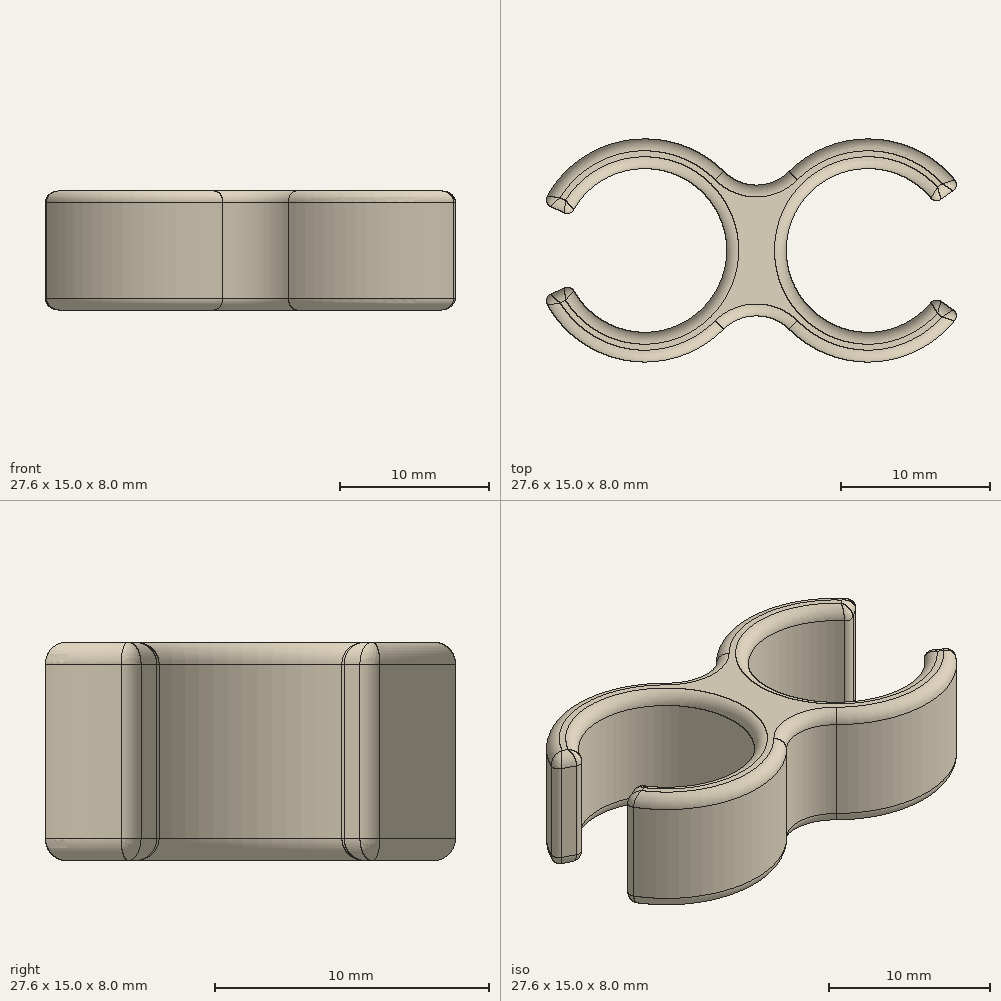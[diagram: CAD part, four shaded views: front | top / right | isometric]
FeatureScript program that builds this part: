
annotation { "Feature Type Name" : "Feature", "Feature Type Description" : "" }
export const myFeature = defineFeature(function(context is Context, id is Id, definition is map)
    precondition{}
    {
        {
            var Q0;
            Q0=qCreatedBy(makeId("Top.planeOp"),FACE);
            var sketch = newSketch(context, id + "F0", { "sketchPlane" : qUnion([Q0])});
            skArc(sketch, "E0", {"start": v(-4.77, -2.73) * mm, "mid": v(5.5, 0) * mm, "end": v(-4.77, 2.73) * mm});
            skArc(sketch, "E1", {"start": v(19.23, 3.52) * mm, "mid": v(9.5, 0) * mm, "end": v(19.23, -3.52) * mm});
            skLineSegment(sketch, "E2", {"start": v(0, 0) * mm, "end": v(18.57, 0) * mm, "construction": true});
            skArc(sketch, "E3.0", {"start": v(-6.55, -3.65) * mm, "mid": v(-1.04, -7.43) * mm, "end": v(5.3, -5.3) * mm});
            skArc(sketch, "E4.0", {"start": v(20.82, 4.73) * mm, "mid": v(15.39, 7.5) * mm, "end": v(9.7, 5.3) * mm});
            skLineSegment(sketch, "E5", {"start": v(7.5, 0) * mm, "end": v(7.5, 7.5) * mm, "construction": true});
            skLineSegment(sketch, "E6", {"start": v(7.5, 0) * mm, "end": v(7.5, -7.5) * mm, "construction": true});
            skArc(sketch, "E7", {"start": v(5.3, 5.3) * mm, "mid": v(7.5, 4.4) * mm, "end": v(9.7, 5.3) * mm});
            skArc(sketch, "E8", {"start": v(9.7, -5.3) * mm, "mid": v(7.5, -4.4) * mm, "end": v(5.3, -5.3) * mm});
            skLineSegment(sketch, "E9", {"start": v(0, 0) * mm, "end": v(-9.83, 0) * mm, "construction": true});
            skLineSegment(sketch, "E10", {"start": v(-5.42, 2.53) * mm, "end": v(-6.33, 2.95) * mm});
            skLineSegment(sketch, "E11", {"start": v(-5.42, -2.53) * mm, "end": v(-6.33, -2.95) * mm});
            skLineSegment(sketch, "E12", {"start": v(19.9, 3.43) * mm, "end": v(20.72, 4) * mm});
            skLineSegment(sketch, "E13", {"start": v(19.9, -3.43) * mm, "end": v(20.72, -4) * mm});
            skPoint(sketch, "E14.visualSharp", {"position": v(-6.8, 3.17) * mm});
            skArc(sketch, "E14.filletArc", {"start": v(-6.55, 3.65) * mm, "mid": v(-6.6, 3.25) * mm, "end": v(-6.33, 2.95) * mm});
            skPoint(sketch, "E15.visualSharp", {"position": v(-4.98, 2.32) * mm});
            skArc(sketch, "E15.filletArc", {"start": v(-5.42, 2.53) * mm, "mid": v(-5.06, 2.5) * mm, "end": v(-4.77, 2.73) * mm});
            skPoint(sketch, "E16.visualSharp", {"position": v(-6.8, -3.17) * mm});
            skArc(sketch, "E16.filletArc", {"start": v(-6.33, -2.95) * mm, "mid": v(-6.6, -3.25) * mm, "end": v(-6.55, -3.65) * mm});
            skPoint(sketch, "E17.visualSharp", {"position": v(-4.98, -2.32) * mm});
            skArc(sketch, "E17.filletArc", {"start": v(-4.77, -2.73) * mm, "mid": v(-5.06, -2.5) * mm, "end": v(-5.42, -2.53) * mm});
            skPoint(sketch, "E18.visualSharp", {"position": v(19.5, -3.15) * mm});
            skArc(sketch, "E18.filletArc", {"start": v(19.9, -3.43) * mm, "mid": v(19.54, -3.34) * mm, "end": v(19.23, -3.52) * mm});
            skPoint(sketch, "E19.visualSharp", {"position": v(21.14, -4.3) * mm});
            skArc(sketch, "E19.filletArc", {"start": v(20.82, -4.73) * mm, "mid": v(20.93, -4.35) * mm, "end": v(20.72, -4) * mm});
            skPoint(sketch, "E20.visualSharp", {"position": v(19.5, 3.15) * mm});
            skArc(sketch, "E20.filletArc", {"start": v(19.23, 3.52) * mm, "mid": v(19.54, 3.34) * mm, "end": v(19.9, 3.43) * mm});
            skPoint(sketch, "E21.visualSharp", {"position": v(21.14, 4.3) * mm});
            skArc(sketch, "E21.filletArc", {"start": v(20.72, 4) * mm, "mid": v(20.93, 4.35) * mm, "end": v(20.82, 4.73) * mm});
            skArc(sketch, "E22.trimOffspring", {"start": v(5.3, 5.3) * mm, "mid": v(-1.04, 7.43) * mm, "end": v(-6.55, 3.65) * mm});
            skArc(sketch, "E23.trimOffspring", {"start": v(9.7, -5.3) * mm, "mid": v(15.39, -7.5) * mm, "end": v(20.82, -4.73) * mm});
            skSolve(sketch);
        }
        {
            var Q0;
            Q0=makeQuery(id+"F0.imprint","IMPRINT",FACE,{"disambiguationData":[TD([[makeQuery(id+"F0.imprint","IMPRINT",EDGE,{"derivedFrom":sQuery(id+"F0.wireOp",EDGE,"E0")}),-1.0]])]});
            extrude(context, id + "F1", {"entities" : qUnion([Q0]), "depth" : 8 * mm, "offsetDistance" : 25 * mm});
        }
        {
            var Q0;
            Q0=makeQuery(id+"F1.opExtrude","CAP_EDGE",EDGE,{"disambiguationData":[OSD([sQuery(id+"F0.wireOp",EDGE,"E7")])],"isStart":false});
            var Q1;
            Q1=makeQuery(id+"F1.opExtrude","CAP_FACE",FACE,{"disambiguationData":[OSD([sQuery(id+"F0.wireOp",EDGE,"E0"),sQuery(id+"F0.wireOp",EDGE,"E1"),sQuery(id+"F0.wireOp",EDGE,"E3.0"),sQuery(id+"F0.wireOp",EDGE,"E4.0"),sQuery(id+"F0.wireOp",EDGE,"E7"),sQuery(id+"F0.wireOp",EDGE,"E8"),sQuery(id+"F0.wireOp",EDGE,"E10"),sQuery(id+"F0.wireOp",EDGE,"E11"),sQuery(id+"F0.wireOp",EDGE,"E12"),sQuery(id+"F0.wireOp",EDGE,"E13"),sQuery(id+"F0.wireOp",EDGE,"E14.filletArc"),sQuery(id+"F0.wireOp",EDGE,"E15.filletArc"),sQuery(id+"F0.wireOp",EDGE,"E16.filletArc"),sQuery(id+"F0.wireOp",EDGE,"E17.filletArc"),sQuery(id+"F0.wireOp",EDGE,"E18.filletArc"),sQuery(id+"F0.wireOp",EDGE,"E19.filletArc"),sQuery(id+"F0.wireOp",EDGE,"E20.filletArc"),sQuery(id+"F0.wireOp",EDGE,"E21.filletArc"),sQuery(id+"F0.wireOp",EDGE,"E22.trimOffspring"),sQuery(id+"F0.wireOp",EDGE,"E23.trimOffspring")])],"isStart":true});
            fillet(context, id + "F2", {"entities" : qUnion([Q0, Q1]), "radius" : 0.8 * mm, "tangentPropagation" : true, "allowEdgeOverflow" : false});
        }
    });
